FCSTD DOCUMENT  (FreeCAD 1.0R39319 (Git))
Label: main-assembly
License: All rights reserved
LicenseURL: http://en.wikipedia.org/wiki/All_rights_reserved
objects: App::Link×62, App::FeaturePython×6, Assembly::AssemblyLink×5, TechDraw::DrawViewImage×4, Assembly::JointGroup×1, Assembly::AssemblyObject×1, TechDraw::DrawSVGTemplate×1, TechDraw::DrawViewAnnotation×1, TechDraw::DrawPage×1
EXTERNAL_REF file=../sub-assemblies/legs.FCStd obj=Assembly
EXTERNAL_REF file=../sub-assemblies/legs.FCStd obj=steel_profile_40x40x400
EXTERNAL_REF file=../sub-assemblies/legs.FCStd obj=steel_profile_40x40x401
EXTERNAL_REF file=../sub-assemblies/legs.FCStd obj=steel_profile_40x40x402
EXTERNAL_REF file=../sub-assemblies/legs.FCStd obj=steel_profile_40x40x403
EXTERNAL_REF file=../sub-assemblies/legs.FCStd obj=steel_profile_40x40x404
EXTERNAL_REF file=../sub-assemblies/legs.FCStd obj=steel_profile_40x40x405
EXTERNAL_REF file=../sub-assemblies/legs.FCStd obj=steel_profile_40x40x406
EXTERNAL_REF file=../sub-assemblies/legs.FCStd obj=steel_profile_40x40x407
EXTERNAL_REF file=../sub-assemblies/legs.FCStd obj=steel_profile_40x40x408
EXTERNAL_REF file=../sub-assemblies/legs.FCStd obj=steel_profile_40x40x411
EXTERNAL_REF file=../sub-assemblies/legs.FCStd obj=steel_profile_40x40x412
EXTERNAL_REF file=../sub-assemblies/legs.FCStd obj=steel_profile_40x40x413
EXTERNAL_REF file=../sub-assemblies/legs.FCStd obj=steel_profile_40x40x414
EXTERNAL_REF file=../sub-assemblies/top-frame.FCStd obj=Assembly
EXTERNAL_REF file=../sub-assemblies/top-frame.FCStd obj=steel_profile_40x40x400
EXTERNAL_REF file=../sub-assemblies/top-frame.FCStd obj=steel_profile_40x40x401
EXTERNAL_REF file=../sub-assemblies/top-frame.FCStd obj=steel_profile_40x40x402
EXTERNAL_REF file=../sub-assemblies/top-frame.FCStd obj=steel_profile_40x40x403
EXTERNAL_REF file=../sub-assemblies/top-frame.FCStd obj=steel_profile_40x40x404
EXTERNAL_REF file=../sub-assemblies/top-frame.FCStd obj=steel_profile_40x40x405
EXTERNAL_REF file=../sub-assemblies/stepper-assembly.FCStd obj=Assembly
EXTERNAL_REF file=../sub-assemblies/stepper-assembly.FCStd obj=nema23_holder
EXTERNAL_REF file=../sub-assemblies/stepper-assembly.FCStd obj=Power_Step___PSM57HS2A54_2P
EXTERNAL_REF file=../sub-assemblies/stepper-assembly.FCStd obj=Coupler_6_35_8mm_Without_Screw
EXTERNAL_REF file=../sub-assemblies/stepper-assembly.FCStd obj=Part
EXTERNAL_REF file=../sub-assemblies/stepper-assembly.FCStd obj=ThreadedRod
EXTERNAL_REF file=../sub-assemblies/legs.FCStd obj=steel_profile_40x40x415
EXTERNAL_REF file=../sub-assemblies/legs.FCStd obj=x_stepper_mounting_profile
EXTERNAL_REF file=../sub-assemblies/stepper-assembly.FCStd obj=x_profile
EXTERNAL_REF file=../sub-assemblies/stepper-assembly.FCStd obj=Anti_Backlash_Nut_TR8x2
EXTERNAL_REF file=../sub-assemblies/stepper-assembly.FCStd obj=Part001
EXTERNAL_REF file=../sub-assemblies/stepper-assembly.FCStd obj=block_MGN9_H009
EXTERNAL_REF file=../sub-assemblies/stepper-assembly.FCStd obj=rail
EXTERNAL_REF file=../sub-assemblies/stepper-assembly.FCStd obj=MGN9_H
EXTERNAL_REF file=../sub-assemblies/stepper-assembly.FCStd obj=Part002
EXTERNAL_REF file=../sub-assemblies/top-frame.FCStd obj=steel_profile_40x40x406
EXTERNAL_REF file=../sub-assemblies/Y-stepper-assembly.FCStd obj=Assembly
EXTERNAL_REF file=../sub-assemblies/Y-stepper-assembly.FCStd obj=nema23_holder
EXTERNAL_REF file=../sub-assemblies/Y-stepper-assembly.FCStd obj=Power_Step___PSM57HS2A54_2P
EXTERNAL_REF file=../sub-assemblies/Y-stepper-assembly.FCStd obj=Coupler_6_35_8mm_Without_Screw
EXTERNAL_REF file=../sub-assemblies/Y-stepper-assembly.FCStd obj=Part
EXTERNAL_REF file=../sub-assemblies/Y-stepper-assembly.FCStd obj=ThreadedRod
EXTERNAL_REF file=../sub-assemblies/Y-stepper-assembly.FCStd obj=Anti_Backlash_Nut_TR8x2
EXTERNAL_REF file=../sub-assemblies/Y-stepper-assembly.FCStd obj=Part001
EXTERNAL_REF file=../sub-assemblies/Y-stepper-assembly.FCStd obj=MGN9_H
EXTERNAL_REF file=../sub-assemblies/Y-stepper-assembly.FCStd obj=Part002
EXTERNAL_REF file=../sub-assemblies/Y-stepper-assembly.FCStd obj=y_profile
EXTERNAL_REF file=../sub-assemblies/Z-stepper-assembly.FCStd obj=Assembly
EXTERNAL_REF file=../sub-assemblies/Z-stepper-assembly.FCStd obj=nema23_holder
EXTERNAL_REF file=../sub-assemblies/Z-stepper-assembly.FCStd obj=Power_Step___PSM57HS2A54_2P
EXTERNAL_REF file=../sub-assemblies/Z-stepper-assembly.FCStd obj=Coupler_6_35_8mm_Without_Screw
EXTERNAL_REF file=../sub-assemblies/Z-stepper-assembly.FCStd obj=Part
EXTERNAL_REF file=../sub-assemblies/Z-stepper-assembly.FCStd obj=ThreadedRod
EXTERNAL_REF file=../sub-assemblies/Z-stepper-assembly.FCStd obj=Anti_Backlash_Nut_TR8x2
EXTERNAL_REF file=../sub-assemblies/Z-stepper-assembly.FCStd obj=Part001
EXTERNAL_REF file=../sub-assemblies/Z-stepper-assembly.FCStd obj=MGN9_H
EXTERNAL_REF file=../sub-assemblies/Z-stepper-assembly.FCStd obj=Part002
EXTERNAL_REF file=../sub-assemblies/Z-stepper-assembly.FCStd obj=_0mm_motor_holder
EXTERNAL_REF file=../sub-assemblies/Z-stepper-assembly.FCStd obj=_0x40x100mm_profile
EXTERNAL_REF file=../sub-assemblies/Z-stepper-assembly.FCStd obj=Screw001
EXTERNAL_REF file=../sub-assemblies/Z-stepper-assembly.FCStd obj=Screw002
EXTERNAL_REF file=../sub-assemblies/Z-stepper-assembly.FCStd obj=M6x90_Screw_Copy
EXTERNAL_REF file=../sub-assemblies/Z-stepper-assembly.FCStd obj=M6x90_Screw_Copy001
EXTERNAL_REF file=../sub-assemblies/Z-stepper-assembly.FCStd obj=M6x90_Screw_Copy002
EXTERNAL_REF file=../sub-assemblies/Y-stepper-assembly.FCStd obj=_0x40x100mm_profile
EXTERNAL_REF file=../sub-assemblies/Y-stepper-assembly.FCStd obj=_0x40x100mm_profile001

FEATURE [App::Link] steel_profile_40x40x400  label="steel-profile-40x40x400"
  LinkPlacement = pos=(0,0,7.8701e-12) rot=(0,0,1;0rad)
  LinkedObject = -> <external ../sub-assemblies/legs.FCStd>#steel_profile_40x40x400
  Placement = pos=(0,0,7.8701e-12) rot=(0,0,1;0rad)
FEATURE [App::Link] steel_profile_40x40x401  label="steel-profile-40x40x401"
  LinkedObject = -> <external ../sub-assemblies/legs.FCStd>#steel_profile_40x40x401
FEATURE [App::Link] steel_profile_40x40x402  label="steel-profile-40x40x402"
  LinkPlacement = pos=(40,40,-9.72909e-07) rot=(0,0.707107,0.707107;3.14159rad)
  LinkedObject = -> <external ../sub-assemblies/legs.FCStd>#steel_profile_40x40x402
  Placement = pos=(40,40,-9.72909e-07) rot=(0,0.707107,0.707107;3.14159rad)
FEATURE [App::Link] steel_profile_40x40x403  label="steel-profile-40x40x403"
  LinkPlacement = pos=(-400,0,400) rot=(4.1e-05,1,0.000414;3.14076rad)
  LinkedObject = -> <external ../sub-assemblies/legs.FCStd>#steel_profile_40x40x403
  Placement = pos=(-400,0,400) rot=(4.1e-05,1,0.000414;3.14076rad)
FEATURE [App::Link] steel_profile_40x40x404  label="steel-profile-40x40x404"
  LinkPlacement = pos=(-440,440,0) rot=(0.99998,0.004685,0.004188;1.57079rad)
  LinkedObject = -> <external ../sub-assemblies/legs.FCStd>#steel_profile_40x40x404
  Placement = pos=(-440,440,0) rot=(0.99998,0.004685,0.004188;1.57079rad)
FEATURE [App::Link] steel_profile_40x40x405  label="steel-profile-40x40x405"
  LinkPlacement = pos=(0,440,0) rot=(0,0,1;0rad)
  LinkedObject = -> <external ../sub-assemblies/legs.FCStd>#steel_profile_40x40x405
  Placement = pos=(0,440,0) rot=(0,0,1;0rad)
FEATURE [App::Link] steel_profile_40x40x406  label="steel-profile-40x40x406"
  LinkPlacement = pos=(0,440,0) rot=(-0.003469,0.999988,-0.003488;4.71178rad)
  LinkedObject = -> <external ../sub-assemblies/legs.FCStd>#steel_profile_40x40x406
  Placement = pos=(0,440,0) rot=(-0.003469,0.999988,-0.003488;4.71178rad)
FEATURE [App::Link] steel_profile_40x40x407  label="steel-profile-40x40x407"
  LinkPlacement = pos=(-9.9e-15,1.7e-15,-3e-16) rot=(0.000745,0.999999,0.000745;4.71239rad)
  LinkedObject = -> <external ../sub-assemblies/legs.FCStd>#steel_profile_40x40x407
  Placement = pos=(-9.9e-15,1.7e-15,-3e-16) rot=(0.000745,0.999999,0.000745;4.71239rad)
FEATURE [App::Link] steel_profile_40x40x408  label="steel-profile-40x40x408"
  LinkPlacement = pos=(-440,440,0) rot=(-0.01966,0.055819,0.998247;0.008893rad)
  LinkedObject = -> <external ../sub-assemblies/legs.FCStd>#steel_profile_40x40x408
  Placement = pos=(-440,440,0) rot=(-0.01966,0.055819,0.998247;0.008893rad)
FEATURE [App::Link] steel_profile_40x40x411  label="steel-profile-40x40x411"
  LinkPlacement = pos=(0,440,360) rot=(0.000611,1,0.000434;4.71234rad)
  LinkedObject = -> <external ../sub-assemblies/legs.FCStd>#steel_profile_40x40x411
  Placement = pos=(0,440,360) rot=(0.000611,1,0.000434;4.71234rad)
FEATURE [App::Link] steel_profile_40x40x412  label="steel-profile-40x40x412"
  LinkPlacement = pos=(0,440,400) rot=(0.714086,0.000272,-0.713488;3.14225rad)
  LinkedObject = -> <external ../sub-assemblies/legs.FCStd>#steel_profile_40x40x412
  Placement = pos=(0,440,400) rot=(0.714086,0.000272,-0.713488;3.14225rad)
FEATURE [App::Link] steel_profile_40x40x413  label="steel-profile-40x40x413"
  LinkPlacement = pos=(0,0,360) rot=(-0.000373,1,0.000455;4.71239rad)
  LinkedObject = -> <external ../sub-assemblies/legs.FCStd>#steel_profile_40x40x413
  Placement = pos=(0,0,360) rot=(-0.000373,1,0.000455;4.71239rad)
FEATURE [App::Link] steel_profile_40x40x414  label="steel-profile-40x40x414"
  LinkPlacement = pos=(0,80,400.402) rot=(0.707403,0.000269,-0.706811;3.14225rad)
  LinkedObject = -> <external ../sub-assemblies/legs.FCStd>#steel_profile_40x40x414
  Placement = pos=(0,80,400.402) rot=(0.707403,0.000269,-0.706811;3.14225rad)
FEATURE [App::Link] steel_profile_40x40x415  label="steel-profile-40x40x415"
  LinkedObject = -> <external ../sub-assemblies/top-frame.FCStd>#steel_profile_40x40x400
FEATURE [App::Link] steel_profile_40x40x416  label="steel-profile-40x40x416"
  LinkPlacement = pos=(440,0,4e-05) rot=(0,0,1;0rad)
  LinkedObject = -> <external ../sub-assemblies/top-frame.FCStd>#steel_profile_40x40x401
  Placement = pos=(440,0,4e-05) rot=(0,0,1;0rad)
FEATURE [App::Link] steel_profile_40x40x417  label="steel-profile-40x40x417"
  LinkPlacement = pos=(0,440,0) rot=(0,0,1;0rad)
  LinkedObject = -> <external ../sub-assemblies/top-frame.FCStd>#steel_profile_40x40x402
  Placement = pos=(0,440,0) rot=(0,0,1;0rad)
FEATURE [App::Link] steel_profile_40x40x418  label="steel-profile-40x40x418"
  LinkPlacement = pos=(440,440,0) rot=(0,0,1;0rad)
  LinkedObject = -> <external ../sub-assemblies/top-frame.FCStd>#steel_profile_40x40x403
  Placement = pos=(440,440,0) rot=(0,0,1;0rad)
FEATURE [App::Link] steel_profile_40x40x419  label="steel-profile-40x40x419"
  LinkPlacement = pos=(40,40,376.43) rot=(0.57735,-0.57735,0.57735;4.18879rad)
  LinkedObject = -> <external ../sub-assemblies/top-frame.FCStd>#steel_profile_40x40x404
  Placement = pos=(40,40,376.43) rot=(0.57735,-0.57735,0.57735;4.18879rad)
FEATURE [App::Link] steel_profile_40x40x420  label="steel-profile-40x40x420"
  LinkPlacement = pos=(440,440,360) rot=(0,-1,0;1.5708rad)
  LinkedObject = -> <external ../sub-assemblies/top-frame.FCStd>#steel_profile_40x40x405
  Placement = pos=(440,440,360) rot=(0,-1,0;1.5708rad)
FEATURE [App::FeaturePython] Joint  label="Parallel"  # Assembly joint (typed FeaturePython)
  Activated = true
  AngleMax = 0
  AngleMin = 0
  Detach1 = false
  Detach2 = false
  Distance = 0
  Distance2 = 0
  EnableAngleMax = false
  EnableAngleMin = false
  EnableLengthMax = false
  EnableLengthMin = false
  JointType = 6 (Parallel)
  LengthMax = 0
  LengthMin = 0
  Placement1 = pos=(40,20,200) rot=(-0.57735,-0.57735,0.57735;2.0944rad)
  Placement2 = pos=(-1e-15,2,0) rot=(0.57735,-0.57735,0.57735;4.18879rad)
  Reference1 = -> Assembly [legs.steel_profile_40x40x400.Body.Face3,legs.steel_profile_40x40x400.Body.Face3]
  Reference2 = -> Assembly [Assembly001.steel_profile_40x40x417.Body.Face7,Assembly001.steel_profile_40x40x417.Body.Vertex15]
FEATURE [App::FeaturePython] Joint001  label="Parallel001"  # Assembly joint (typed FeaturePython)
  Activated = true
  AngleMax = 0
  AngleMin = 0
  Detach1 = false
  Detach2 = false
  Distance = 0
  Distance2 = 0
  EnableAngleMax = false
  EnableAngleMin = false
  EnableLengthMax = false
  EnableLengthMin = false
  JointType = 6 (Parallel)
  LengthMax = 0
  LengthMin = 0
  Placement1 = pos=(20,-9e-16,200) rot=(-1,0,0;1.5708rad)
  Placement2 = pos=(2,40,0) rot=(0,-0.707107,0.707107;3.14159rad)
  Reference1 = -> Assembly [legs.steel_profile_40x40x400.Body.Face1,legs.steel_profile_40x40x400.Body.Face1]
  Reference2 = -> Assembly [Assembly001.steel_profile_40x40x417.Body.Face5,Assembly001.steel_profile_40x40x417.Body.Vertex11]
FEATURE [App::FeaturePython] Joint002  label="Distance"  # Assembly joint (typed FeaturePython)
  Activated = true
  AngleMax = 0
  AngleMin = 0
  Detach1 = false
  Detach2 = false
  Distance = 0
  Distance2 = 0
  EnableAngleMax = false
  EnableAngleMin = false
  EnableLengthMax = false
  EnableLengthMin = false
  JointType = 5 (Distance)
  LengthMax = 0
  LengthMin = 0
  Placement1 = pos=(20,20,0) rot=(0,0,1;0rad)
  Placement2 = pos=(20,20,400) rot=(0,0,1;0rad)
  Reference1 = -> Assembly [Assembly001.steel_profile_40x40x417.Body.Face13,Assembly001.steel_profile_40x40x417.Body.Vertex21]
  Reference2 = -> Assembly [legs.steel_profile_40x40x400.Body.Face14,legs.steel_profile_40x40x400.Body.Vertex22]
FEATURE [App::FeaturePython] Joint003  label="Distance001"  # Assembly joint (typed FeaturePython)
  Activated = true
  AngleMax = 0
  AngleMin = 0
  Detach1 = false
  Detach2 = false
  Distance = 0
  Distance2 = 0
  EnableAngleMax = false
  EnableAngleMin = false
  EnableLengthMax = false
  EnableLengthMin = false
  JointType = 5 (Distance)
  LengthMax = 0
  LengthMin = 0
  Placement1 = pos=(20,-9e-16,200) rot=(-1,0,0;1.5708rad)
  Placement2 = pos=(20,40,200) rot=(0,-0.707107,0.707107;3.14159rad)
  Reference1 = -> Assembly [legs.steel_profile_40x40x400.Body.Face1,legs.steel_profile_40x40x400.Body.Vertex4]
  Reference2 = -> Assembly [Assembly001.steel_profile_40x40x417.Body.Face5,Assembly001.steel_profile_40x40x417.Body.Vertex11]
FEATURE [App::Link] nema23_holder  label="nema23-holder"
  LinkPlacement = pos=(0,0,0) rot=(-0.953069,0,-0.302943;2e-06rad)
  LinkedObject = -> <external ../sub-assemblies/stepper-assembly.FCStd>#nema23_holder
  Placement = pos=(0,0,0) rot=(-0.953069,0,-0.302943;2e-06rad)
FEATURE [App::Link] Power_Step___PSM57HS2A54_2P  label="Power Step - PSM57HS2A54-2P002"
  LinkPlacement = pos=(32.5,44.5,35.5) rot=(-2e-06,1,-4e-06;1.5708rad)
  LinkedObject = -> <external ../sub-assemblies/stepper-assembly.FCStd>#Power_Step___PSM57HS2A54_2P
  Placement = pos=(32.5,44.5,35.5) rot=(-2e-06,1,-4e-06;1.5708rad)
FEATURE [App::Link] Coupler_6_35_8mm_Without_Screw  label="Coupler 6.35-8mm Without Screw001"
  LinkPlacement = pos=(32.5,96.0278,35.5) rot=(0.993786,0.078707,-0.078701;1.57705rad)
  LinkedObject = -> <external ../sub-assemblies/stepper-assembly.FCStd>#Coupler_6_35_8mm_Without_Screw
  Placement = pos=(32.5,96.0278,35.5) rot=(0.993786,0.078707,-0.078701;1.57705rad)
FEATURE [App::Link] Part  label="bearing-support"
  LinkPlacement = pos=(32.498,479.614,35.5061) rot=(-1,-3e-06,3e-06;1.57078rad)
  LinkedObject = -> <external ../sub-assemblies/stepper-assembly.FCStd>#Part
  Placement = pos=(32.498,479.614,35.5061) rot=(-1,-3e-06,3e-06;1.57078rad)
FEATURE [App::Link] ThreadedRod  label="M8x400-ThreadedRod"
  LinkPlacement = pos=(32.5,94.614,35.5) rot=(-0.04014,0.706542,-0.706531;3.22182rad)
  LinkedObject = -> <external ../sub-assemblies/stepper-assembly.FCStd>#ThreadedRod
  Placement = pos=(32.5,94.614,35.5) rot=(-0.04014,0.706542,-0.706531;3.22182rad)
FEATURE [App::Link] steel_profile_40x40x421  label="steel-profile-40x40x421"
  LinkPlacement = pos=(-440,40,418.3) rot=(-0.999999,0,0;1.5708rad)
  LinkedObject = -> <external ../sub-assemblies/legs.FCStd>#steel_profile_40x40x415
  Placement = pos=(-440,40,418.3) rot=(-0.999999,0,0;1.5708rad)
FEATURE [App::Link] x_stepper_mounting_profile  label="x-stepper-mounting-profile"
  LinkPlacement = pos=(1.563e-13,440,354.54) rot=(0,0,-1;1.5708rad)
  LinkedObject = -> <external ../sub-assemblies/legs.FCStd>#x_stepper_mounting_profile
  Placement = pos=(1.563e-13,440,354.54) rot=(0,0,-1;1.5708rad)
FEATURE [Assembly::AssemblyLink] legs
  Group = -> [steel_profile_40x40x400,steel_profile_40x40x401,steel_profile_40x40x402,steel_profile_40x40x403,steel_profile_40x40x404,steel_profile_40x40x405,steel_profile_40x40x406,steel_profile_40x40x407,steel_profile_40x40x408,steel_profile_40x40x411,steel_profile_40x40x412,steel_profile_40x40x413,steel_profile_40x40x414,steel_profile_40x40x421,x_stepper_mounting_profile]
  LinkedObject = -> <external ../sub-assemblies/legs.FCStd>#Assembly
  Origin = -> Origin001
  Rigid = true
FEATURE [App::FeaturePython] GroundedJoint  # Assembly grounded joint (typed FeaturePython)
  ObjectToGround = -> legs
FEATURE [App::Link] x_profile  label="x-profile"
  LinkPlacement = pos=(-167.5,276.601,55.7999) rot=(-0.577347,0.577348,0.577356;2.09438rad)
  LinkedObject = -> <external ../sub-assemblies/stepper-assembly.FCStd>#x_profile
  Placement = pos=(-167.5,276.601,55.7999) rot=(-0.577347,0.577348,0.577356;2.09438rad)
FEATURE [App::Link] Anti_Backlash_Nut_TR8x2  label="Anti-Backlash_Nut_TR8x005"
  LinkPlacement = pos=(32.5,316.91,35.5) rot=(0,1,0;0rad)
  LinkedObject = -> <external ../sub-assemblies/stepper-assembly.FCStd>#Anti_Backlash_Nut_TR8x2
  Placement = pos=(32.5,316.91,35.5) rot=(0,1,0;0rad)
FEATURE [App::Link] Part001  label="Nut-TR8"
  LinkPlacement = pos=(32.4991,261.601,35.5026) rot=(-0.577351,0.577355,-0.577345;4.18878rad)
  LinkedObject = -> <external ../sub-assemblies/stepper-assembly.FCStd>#Part001
  Placement = pos=(32.4991,261.601,35.5026) rot=(-0.577351,0.577355,-0.577345;4.18878rad)
FEATURE [App::Link] block_MGN9_H009  label="block-MGN9-H010"
  LinkPlacement = pos=(214.983,296.784,11.8004) rot=(1,-1e-06,-1e-06;1.57081rad)
  LinkedObject = -> <external ../sub-assemblies/stepper-assembly.FCStd>#block_MGN9_H009
  Placement = pos=(214.983,296.784,11.8004) rot=(1,-1e-06,-1e-06;1.57081rad)
FEATURE [App::Link] rail  label="rail001"
  LinkPlacement = pos=(214.965,441.284,9.01518) rot=(1,-1e-06,-1e-06;1.57081rad)
  LinkedObject = -> <external ../sub-assemblies/stepper-assembly.FCStd>#rail
  Placement = pos=(214.965,441.284,9.01518) rot=(1,-1e-06,-1e-06;1.57081rad)
FEATURE [App::Link] MGN9_H  label="block-MGN9-H009"
  LinkPlacement = pos=(-149.71,296.602,11.8002) rot=(1e-06,0.781989,0.782002;3.14159rad)
  LinkedObject = -> <external ../sub-assemblies/stepper-assembly.FCStd>#MGN9_H
  Placement = pos=(-149.71,296.602,11.8002) rot=(1e-06,0.781989,0.782002;3.14159rad)
FEATURE [App::Link] Part002  label="rail"
  LinkPlacement = pos=(-149.691,441.102,8.99001) rot=(1,-1e-06,-1e-06;1.57081rad)
  LinkedObject = -> <external ../sub-assemblies/stepper-assembly.FCStd>#Part002
  Placement = pos=(-149.691,441.102,8.99001) rot=(1,-1e-06,-1e-06;1.57081rad)
FEATURE [Assembly::AssemblyLink] stepper_assembly  label="stepper-assembly"
  Group = -> [nema23_holder,Power_Step___PSM57HS2A54_2P,Coupler_6_35_8mm_Without_Screw,Part,ThreadedRod,x_profile,Anti_Backlash_Nut_TR8x2,Part001,block_MGN9_H009,rail,MGN9_H,Part002]
  LinkedObject = -> <external ../sub-assemblies/stepper-assembly.FCStd>#Assembly
  Origin = -> Origin003
  Placement = pos=(60,207.5,394.54) rot=(0,0,1;1.5708rad)
  Rigid = true
FEATURE [App::Link] steel_profile_40x40x422  label="steel-profile-40x40x422"
  LinkPlacement = pos=(3,40,400) rot=(1,0,0;4.71239rad)
  LinkedObject = -> <external ../sub-assemblies/top-frame.FCStd>#steel_profile_40x40x406
  Placement = pos=(3,40,400) rot=(1,0,0;4.71239rad)
FEATURE [Assembly::AssemblyLink] Assembly001  label="top-frame"
  Group = -> [steel_profile_40x40x415,steel_profile_40x40x416,steel_profile_40x40x417,steel_profile_40x40x418,steel_profile_40x40x419,steel_profile_40x40x420,steel_profile_40x40x422]
  LinkedObject = -> <external ../sub-assemblies/top-frame.FCStd>#Assembly
  Origin = -> Origin002
  Placement = pos=(40,480,400) rot=(0,0,1;3.14159rad)
  Rigid = true
FEATURE [App::Link] nema23_holder001  label="nema23-holder001"
  LinkPlacement = pos=(0,0,0) rot=(-0.952988,0,-0.302917;2e-06rad)
  LinkedObject = -> <external ../sub-assemblies/Y-stepper-assembly.FCStd>#nema23_holder
  Placement = pos=(0,0,0) rot=(-0.952988,0,-0.302917;2e-06rad)
FEATURE [App::Link] Power_Step___PSM57HS2A54_2P001  label="Power Step - PSM57HS2A54-2P003"
  LinkPlacement = pos=(32.5,44.5,35.5) rot=(-2e-06,1,-4e-06;1.5708rad)
  LinkedObject = -> <external ../sub-assemblies/Y-stepper-assembly.FCStd>#Power_Step___PSM57HS2A54_2P
  Placement = pos=(32.5,44.5,35.5) rot=(-2e-06,1,-4e-06;1.5708rad)
FEATURE [App::Link] Coupler_6_35_8mm_Without_Screw001  label="Coupler 6.35-8mm Without Screw002"
  LinkPlacement = pos=(32.5,96.0278,35.5) rot=(0.993786,0.078707,-0.078701;1.57705rad)
  LinkedObject = -> <external ../sub-assemblies/Y-stepper-assembly.FCStd>#Coupler_6_35_8mm_Without_Screw
  Placement = pos=(32.5,96.0278,35.5) rot=(0.993786,0.078707,-0.078701;1.57705rad)
FEATURE [App::Link] Part003  label="bearing-support001"
  LinkPlacement = pos=(32.498,479.614,35.5061) rot=(-1,-3e-06,3e-06;1.57078rad)
  LinkedObject = -> <external ../sub-assemblies/Y-stepper-assembly.FCStd>#Part
  Placement = pos=(32.498,479.614,35.5061) rot=(-1,-3e-06,3e-06;1.57078rad)
FEATURE [App::Link] ThreadedRod001  label="M8x400-ThreadedRod001"
  LinkPlacement = pos=(32.5,94.614,35.5) rot=(-0.04014,0.706542,-0.706531;3.22182rad)
  LinkedObject = -> <external ../sub-assemblies/Y-stepper-assembly.FCStd>#ThreadedRod
  Placement = pos=(32.5,94.614,35.5) rot=(-0.04014,0.706542,-0.706531;3.22182rad)
FEATURE [App::Link] Anti_Backlash_Nut_TR8x003  label="Anti-Backlash_Nut_TR8x006"
  LinkPlacement = pos=(32.5,316.91,35.5) rot=(0,1,0;0rad)
  LinkedObject = -> <external ../sub-assemblies/Y-stepper-assembly.FCStd>#Anti_Backlash_Nut_TR8x2
  Placement = pos=(32.5,316.91,35.5) rot=(0,1,0;0rad)
FEATURE [App::Link] Part004  label="Nut-TR009"
  LinkPlacement = pos=(32.4991,261.601,35.5026) rot=(0.577353,-0.577352,0.577346;2.09441rad)
  LinkedObject = -> <external ../sub-assemblies/Y-stepper-assembly.FCStd>#Part001
  Placement = pos=(32.4991,261.601,35.5026) rot=(0.577353,-0.577352,0.577346;2.09441rad)
FEATURE [App::Link] MGN9_H001  label="block-MGN9-H011"
  LinkPlacement = pos=(8.50001,296.601,3.00315) rot=(-0.595349,-0.595353,-0.595359;2.09438rad)
  LinkedObject = -> <external ../sub-assemblies/Y-stepper-assembly.FCStd>#MGN9_H
  Placement = pos=(8.50001,296.601,3.00315) rot=(-0.595349,-0.595353,-0.595359;2.09438rad)
FEATURE [App::Link] Part005  label="rail002"
  LinkPlacement = pos=(5.68728,190.892,3.01962) rot=(0.595351,0.595349,0.595361;4.1888rad)
  LinkedObject = -> <external ../sub-assemblies/Y-stepper-assembly.FCStd>#Part002
  Placement = pos=(5.68728,190.892,3.01962) rot=(0.595351,0.595349,0.595361;4.1888rad)
FEATURE [App::FeaturePython] Joint004  label="Distance002"  # Assembly joint (typed FeaturePython)
  Activated = true
  AngleMax = 0
  AngleMin = 0
  Detach1 = false
  Detach2 = false
  Distance = 0
  Distance2 = 0
  EnableAngleMax = false
  EnableAngleMin = false
  EnableLengthMax = false
  EnableLengthMin = false
  JointType = 5 (Distance)
  LengthMax = 0
  LengthMin = 0
  Placement1 = pos=(20,-9e-16,200) rot=(-1,0,0;1.5708rad)
  Placement2 = pos=(32.5,36.1951,0) rot=(0,0,1;0rad)
  Reference1 = -> Assembly [Assembly001.steel_profile_40x40x419.Body.Face1,Assembly001.steel_profile_40x40x419.Body.Vertex1]
  Reference2 = -> Assembly [Y_stepper_assembly.nema23_holder001.Body.Face15,Y_stepper_assembly.nema23_holder001.Body.Edge13]
FEATURE [Assembly::JointGroup] Joints
  Group = -> [GroundedJoint,Joint,Joint001,Joint002,Joint003,Joint004]
FEATURE [App::Link] y_profile  label="y-profile"
  LinkPlacement = pos=(52.4989,316.604,-164.497) rot=(-2e-06,0.729162,-0.72915;3.14159rad)
  LinkedObject = -> <external ../sub-assemblies/Y-stepper-assembly.FCStd>#y_profile
  Placement = pos=(52.4989,316.604,-164.497) rot=(-2e-06,0.729162,-0.72915;3.14159rad)
FEATURE [App::Link] nema23_holder002  label="nema23-holder002"
  LinkPlacement = pos=(-8e-15,0,5.51e-14) rot=(-0.953074,-1.1e-05,-0.302948;2e-06rad)
  LinkedObject = -> <external ../sub-assemblies/Z-stepper-assembly.FCStd>#nema23_holder
  Placement = pos=(-8e-15,0,5.51e-14) rot=(-0.953074,-1.1e-05,-0.302948;2e-06rad)
FEATURE [App::Link] Power_Step___PSM57HS2A54_2P002  label="Power Step - PSM57HS2A54-2P004"
  LinkPlacement = pos=(32.5,44.5,35.5) rot=(-2e-06,1,-4e-06;1.5708rad)
  LinkedObject = -> <external ../sub-assemblies/Z-stepper-assembly.FCStd>#Power_Step___PSM57HS2A54_2P
  Placement = pos=(32.5,44.5,35.5) rot=(-2e-06,1,-4e-06;1.5708rad)
FEATURE [App::Link] Coupler_6_35_8mm_Without_Screw002  label="Coupler 6.35-8mm Without Screw003"
  LinkPlacement = pos=(32.5,96.0278,35.5) rot=(0.993786,0.078707,-0.078701;1.57705rad)
  LinkedObject = -> <external ../sub-assemblies/Z-stepper-assembly.FCStd>#Coupler_6_35_8mm_Without_Screw
  Placement = pos=(32.5,96.0278,35.5) rot=(0.993786,0.078707,-0.078701;1.57705rad)
FEATURE [App::Link] Part006  label="bearing-support002"
  LinkPlacement = pos=(32.498,479.614,35.5061) rot=(-1,-3e-06,3e-06;1.57078rad)
  LinkedObject = -> <external ../sub-assemblies/Z-stepper-assembly.FCStd>#Part
  Placement = pos=(32.498,479.614,35.5061) rot=(-1,-3e-06,3e-06;1.57078rad)
FEATURE [App::Link] ThreadedRod002  label="M8x400-ThreadedRod002"
  LinkPlacement = pos=(32.5,94.614,35.5) rot=(-0.04014,0.706542,-0.706531;3.22182rad)
  LinkedObject = -> <external ../sub-assemblies/Z-stepper-assembly.FCStd>#ThreadedRod
  Placement = pos=(32.5,94.614,35.5) rot=(-0.04014,0.706542,-0.706531;3.22182rad)
FEATURE [App::Link] Anti_Backlash_Nut_TR8x004  label="Anti-Backlash_Nut_TR8x007"
  LinkPlacement = pos=(32.5,316.91,35.5) rot=(0,1,0;0rad)
  LinkedObject = -> <external ../sub-assemblies/Z-stepper-assembly.FCStd>#Anti_Backlash_Nut_TR8x2
  Placement = pos=(32.5,316.91,35.5) rot=(0,1,0;0rad)
FEATURE [App::Link] Part007  label="Nut-TR010"
  LinkPlacement = pos=(32.4991,261.601,35.5026) rot=(0.577353,-0.577352,0.577346;2.09441rad)
  LinkedObject = -> <external ../sub-assemblies/Z-stepper-assembly.FCStd>#Part001
  Placement = pos=(32.4991,261.601,35.5026) rot=(0.577353,-0.577352,0.577346;2.09441rad)
FEATURE [App::Link] MGN9_H002  label="block-MGN9-H012"
  LinkPlacement = pos=(33.1028,297.601,10.4187) rot=(-1e-06,-0.707104,-0.70711;3.1416rad)
  LinkedObject = -> <external ../sub-assemblies/Z-stepper-assembly.FCStd>#MGN9_H
  Placement = pos=(33.1028,297.601,10.4187) rot=(-1e-06,-0.707104,-0.70711;3.1416rad)
FEATURE [App::Link] Part008  label="rail003"
  LinkPlacement = pos=(33.0843,191.891,7.60456) rot=(1e-06,0.707101,0.707112;3.14159rad)
  LinkedObject = -> <external ../sub-assemblies/Z-stepper-assembly.FCStd>#Part002
  Placement = pos=(33.0843,191.891,7.60456) rot=(1e-06,0.707101,0.707112;3.14159rad)
FEATURE [App::Link] _0mm_motor_holder  label="80mm-motor-holder"
  LinkPlacement = pos=(34.5,276.5,55) rot=(0,0.707107,0.707107;3.14159rad)
  LinkedObject = -> <external ../sub-assemblies/Z-stepper-assembly.FCStd>#_0mm_motor_holder
  Placement = pos=(34.5,276.5,55) rot=(0,0.707107,0.707107;3.14159rad)
FEATURE [App::Link] _0x40x100mm_profile  label="40x40x100mm-profile"
  LinkPlacement = pos=(84.5,276.5,15) rot=(0,-1,0;1.5708rad)
  LinkedObject = -> <external ../sub-assemblies/Z-stepper-assembly.FCStd>#_0x40x100mm_profile
  Placement = pos=(84.5,276.5,15) rot=(0,-1,0;1.5708rad)
FEATURE [App::Link] Screw001  label="M6x90-Screw"
  LinkPlacement = pos=(-10.5,282.5,134.5) rot=(0.619938,-0.784651,0;0rad)
  LinkedObject = -> <external ../sub-assemblies/Z-stepper-assembly.FCStd>#Screw001
  Placement = pos=(-10.5,282.5,134.5) rot=(0.619938,-0.784651,0;0rad)
FEATURE [App::Link] Screw002  label="M6x90-Screw001"
  LinkPlacement = pos=(-10.5,312.5,134.5) rot=(0.619938,-0.784651,0;0rad)
  LinkedObject = -> <external ../sub-assemblies/Z-stepper-assembly.FCStd>#Screw002
  Placement = pos=(-10.5,312.5,134.5) rot=(0.619938,-0.784651,0;0rad)
FEATURE [App::Link] M6x90_Screw_Copy
  LinkPlacement = pos=(79.5,282.5,134.6) rot=(0,0,1;3.14159rad)
  LinkedObject = -> <external ../sub-assemblies/Z-stepper-assembly.FCStd>#M6x90_Screw_Copy
  Placement = pos=(79.5,282.5,134.6) rot=(0,0,1;3.14159rad)
FEATURE [App::Link] M6x90_Screw_Copy001
  LinkPlacement = pos=(79.5,312.5,134.6) rot=(0,0,1;3.14159rad)
  LinkedObject = -> <external ../sub-assemblies/Z-stepper-assembly.FCStd>#M6x90_Screw_Copy001
  Placement = pos=(79.5,312.5,134.6) rot=(0,0,1;3.14159rad)
FEATURE [App::Link] M6x90_Screw_Copy002
  LinkPlacement = pos=(-10.5,282.5,134.5) rot=(0.619938,-0.784651,0;0rad)
  LinkedObject = -> <external ../sub-assemblies/Z-stepper-assembly.FCStd>#M6x90_Screw_Copy002
  Placement = pos=(-10.5,282.5,134.5) rot=(0.619938,-0.784651,0;0rad)
FEATURE [Assembly::AssemblyLink] Z_stepper_assembly  label="Z-stepper-assembly"
  Group = -> [nema23_holder002,Power_Step___PSM57HS2A54_2P002,Coupler_6_35_8mm_Without_Screw002,Part006,ThreadedRod002,Anti_Backlash_Nut_TR8x004,Part007,MGN9_H002,Part008,_0mm_motor_holder,_0x40x100mm_profile,Screw001,Screw002,M6x90_Screw_Copy,M6x90_Screw_Copy001,M6x90_Screw_Copy002]
  LinkedObject = -> <external ../sub-assemblies/Z-stepper-assembly.FCStd>#Assembly
  Origin = -> Origin005
  Placement = pos=(-48.7667,173.258,1086.28) rot=(-0.57735,-0.57735,0.57735;2.0944rad)
  Rigid = true
FEATURE [App::Link] _0x40x100mm_profile001  label="40x40x100mm-profile001"
  LinkPlacement = pos=(8.7489,348.05,235.362) rot=(1,0,0;1.5708rad)
  LinkedObject = -> <external ../sub-assemblies/Y-stepper-assembly.FCStd>#_0x40x100mm_profile
  Placement = pos=(8.7489,348.05,235.362) rot=(1,0,0;1.5708rad)
FEATURE [App::Link] _0x40x100mm_profile002  label="40x40x100mm-profile002"
  LinkPlacement = pos=(32,243,-164) rot=(-1,0,0;1.5708rad)
  LinkedObject = -> <external ../sub-assemblies/Y-stepper-assembly.FCStd>#_0x40x100mm_profile001
  Placement = pos=(32,243,-164) rot=(-1,0,0;1.5708rad)
FEATURE [Assembly::AssemblyLink] Y_stepper_assembly  label="Y-stepper-assembly"
  Group = -> [nema23_holder001,Power_Step___PSM57HS2A54_2P001,Coupler_6_35_8mm_Without_Screw001,Part003,ThreadedRod001,Anti_Backlash_Nut_TR8x003,Part004,MGN9_H001,Part005,y_profile,_0x40x100mm_profile001,_0x40x100mm_profile002]
  LinkedObject = -> <external ../sub-assemblies/Y-stepper-assembly.FCStd>#Assembly
  Origin = -> Origin004
  Placement = pos=(-0.612144,502.308,776.43) rot=(0,1e-06,1;3.14159rad)
  Rigid = true
FEATURE [Assembly::AssemblyObject] Assembly
  Group = -> [Joints,legs,GroundedJoint,Assembly001,Joint,Joint001,Joint002,Joint003,stepper_assembly,Y_stepper_assembly,Joint004,Z_stepper_assembly]
  Origin = -> Origin
  Type = Assembly
FEATURE [TechDraw::DrawSVGTemplate] Template
  Height = 210
  Orientation = 1
  Template = <path>
  Width = 297
FEATURE [TechDraw::DrawViewImage] ActiveView001  label="Y"
  Height = 102.4
  ImageFile = <userpath>/.cache/FreeCAD/Cache/FreeCAD_Doc_1507e429-804d-4e93-ae59-f7ba2e4ac061_45bff6_36913/PageActiveView001rUnWWh.png
  LockPosition = false
  Rotation = 0
  ScaleType = 2
  Width = 128
  X = 254.231
  Y = 68.2217
FEATURE [TechDraw::DrawViewImage] ActiveView002  label="Z"
  Height = 102.4
  ImageFile = <userpath>/.cache/FreeCAD/Cache/FreeCAD_Doc_1507e429-804d-4e93-ae59-f7ba2e4ac061_df227c_36913/PageActiveView5mA7Qo.png
  LockPosition = false
  Rotation = 0
  ScaleType = 2
  Width = 128
  X = 175.736
  Y = 60.7246
FEATURE [TechDraw::DrawViewImage] ActiveView  label="X"
  Height = 102.4
  ImageFile = <userpath>/.cache/FreeCAD/Cache/FreeCAD_Doc_1507e429-804d-4e93-ae59-f7ba2e4ac061_0c7716_36913/PageActiveViewThDkJc.png
  LockPosition = false
  Rotation = 0
  ScaleType = 2
  Width = 128
  X = 216.072
  Y = 162.108
FEATURE [TechDraw::DrawViewImage] ActiveView003
  Height = 102.4
  ImageFile = <userpath>/.cache/FreeCAD/Cache/FreeCAD_Doc_a727402a-c459-441b-822e-c6c33594917e_9b285e_36913/PageActiveView003J3glPR.png
  LockPosition = false
  Rotation = 0
  Scale = 2
  ScaleType = 2
  Width = 128
  X = 64.5788
  Y = 92.8871
FEATURE [TechDraw::DrawViewAnnotation] Annotation
  Font = osifont
  LineSpace = 100
  LockPosition = false
  MaxWidth = -1
  Rotation = 0
  ScaleType = 0
  Text = VE1 CNC mill | Open Hardware CERN-OHL-S version 2
  TextSize = 7
  TextStyle = 0
  X = 81.2526
  Y = 194.504
FEATURE [TechDraw::DrawPage] Page
  KeepUpdated = true
  NextBalloonIndex = 1
  ProjectionType = 0
  Template = -> Template
  Views = -> [ActiveView001,ActiveView002,ActiveView,ActiveView003,Annotation]
note: 1 file-system path scrubbed to <path> (originals preserved in the JSON sidecar)

RESOLVED EXTERNAL PARTS (link-assembly join: the EXTERNAL_REF files above that resolve inside this repo's crawl, each included once):
---- part ../sub-assemblies/legs.FCStd = doc fcstd_d6a536308a57 ----
FCSTD DOCUMENT  (FreeCAD 1.0R39319 (Git))
Label: legs
License: All rights reserved
LicenseURL: http://en.wikipedia.org/wiki/All_rights_reserved
objects: App::FeaturePython×23, App::Link×15, Assembly::JointGroup×1, Assembly::AssemblyObject×1
EXTERNAL_REF file=../parts/steel-profile-40x40x400.FCStd obj=Part
EXTERNAL_REF file=../parts/x-stepper-mounting-profile.FCStd obj=Part

FEATURE [App::Link] steel_profile_40x40x400  label="steel-profile-40x40x400"
  LinkPlacement = pos=(0,0,7.8701e-12) rot=(0,0,1;0rad)
  LinkedObject = -> <external ../parts/steel-profile-40x40x400.FCStd>#Part
  Placement = pos=(0,0,7.8701e-12) rot=(0,0,1;0rad)
FEATURE [App::FeaturePython] GroundedJoint  # Assembly grounded joint (typed FeaturePython)
  ObjectToGround = -> steel_profile_40x40x400
  Placement = pos=(0,0,7.8701e-12) rot=(0,0,1;0rad)
FEATURE [App::Link] steel_profile_40x40x401  label="steel-profile-40x40x401"
  LinkedObject = -> <external ../parts/steel-profile-40x40x400.FCStd>#Part
FEATURE [App::Link] steel_profile_40x40x402  label="steel-profile-40x40x402"
  LinkPlacement = pos=(40,40,-9.72909e-07) rot=(0,0.707107,0.707107;3.14159rad)
  LinkedObject = -> <external ../parts/steel-profile-40x40x400.FCStd>#Part
  Placement = pos=(40,40,-9.72909e-07) rot=(0,0.707107,0.707107;3.14159rad)
FEATURE [App::Link] steel_profile_40x40x403  label="steel-profile-40x40x403"
  LinkPlacement = pos=(-400,0,400) rot=(4.1e-05,1,0.000414;3.14076rad)
  LinkedObject = -> <external ../parts/steel-profile-40x40x400.FCStd>#Part
  Placement = pos=(-400,0,400) rot=(4.1e-05,1,0.000414;3.14076rad)
FEATURE [App::Link] steel_profile_40x40x404  label="steel-profile-40x40x404"
  LinkPlacement = pos=(-440,440,0) rot=(0.99998,0.004685,0.004188;1.57079rad)
  LinkedObject = -> <external ../parts/steel-profile-40x40x400.FCStd>#Part
  Placement = pos=(-440,440,0) rot=(0.99998,0.004685,0.004188;1.57079rad)
FEATURE [App::Link] steel_profile_40x40x405  label="steel-profile-40x40x405"
  LinkPlacement = pos=(0,440,0) rot=(0,0,1;0rad)
  LinkedObject = -> <external ../parts/steel-profile-40x40x400.FCStd>#Part
  Placement = pos=(0,440,0) rot=(0,0,1;0rad)
FEATURE [App::Link] steel_profile_40x40x406  label="steel-profile-40x40x406"
  LinkPlacement = pos=(0,440,0) rot=(-0.003469,0.999988,-0.003488;4.71178rad)
  LinkedObject = -> <external ../parts/steel-profile-40x40x400.FCStd>#Part
  Placement = pos=(0,440,0) rot=(-0.003469,0.999988,-0.003488;4.71178rad)
FEATURE [App::Link] steel_profile_40x40x407  label="steel-profile-40x40x407"
  LinkPlacement = pos=(-9.9e-15,1.7e-15,-3e-16) rot=(0.000745,0.999999,0.000745;4.71239rad)
  LinkedObject = -> <external ../parts/steel-profile-40x40x400.FCStd>#Part
  Placement = pos=(-9.9e-15,1.7e-15,-3e-16) rot=(0.000745,0.999999,0.000745;4.71239rad)
FEATURE [App::FeaturePython] GroundedJoint001  # Assembly grounded joint (typed FeaturePython)
  ObjectToGround = -> steel_profile_40x40x402
  Placement = pos=(40,40,-9.72909e-07) rot=(0,0.707107,0.707107;3.14159rad)
FEATURE [App::FeaturePython] GroundedJoint002  # Assembly grounded joint (typed FeaturePython)
  ObjectToGround = -> steel_profile_40x40x407
  Placement = pos=(-9.9e-15,1.7e-15,-3e-16) rot=(0.000745,0.999999,0.000745;4.71239rad)
FEATURE [App::FeaturePython] GroundedJoint003  # Assembly grounded joint (typed FeaturePython)
  ObjectToGround = -> steel_profile_40x40x405
  Placement = pos=(8.20807e-06,440,-1.75932e-05) rot=(0,0,1;0rad)
FEATURE [App::FeaturePython] GroundedJoint004  # Assembly grounded joint (typed FeaturePython)
  ObjectToGround = -> steel_profile_40x40x406
  Placement = pos=(3.27425e-05,440,1.2557e-05) rot=(-0.003469,0.999988,-0.003488;4.71178rad)
FEATURE [App::FeaturePython] Joint  label="Distance"  # Assembly joint (typed FeaturePython)
  Activated = true
  AngleMax = 0
  AngleMin = 0
  Detach1 = false
  Detach2 = false
  Distance = 0
  Distance2 = 0
  EnableAngleMax = false
  EnableAngleMin = false
  EnableLengthMax = false
  EnableLengthMin = false
  JointType = 5 (Distance)
  LengthMax = 0
  LengthMin = 0
  Placement1 = pos=(40,20,200) rot=(-0.57735,-0.57735,0.57735;2.0944rad)
  Placement2 = pos=(20,20,400) rot=(0,0,1;0rad)
  Reference1 = -> Assembly [steel_profile_40x40x404.Body.Face3,steel_profile_40x40x404.Body.Vertex5]
  Reference2 = -> Assembly [steel_profile_40x40x406.Body.Face14,steel_profile_40x40x406.Body.Vertex18]
FEATURE [App::FeaturePython] Joint001  label="Distance001"  # Assembly joint (typed FeaturePython)
  Activated = true
  AngleMax = 0
  AngleMin = 0
  Detach1 = false
  Detach2 = false
  Distance = 0
  Distance2 = 0
  EnableAngleMax = false
  EnableAngleMin = false
  EnableLengthMax = false
  EnableLengthMin = false
  JointType = 5 (Distance)
  LengthMax = 0
  LengthMin = 0
  Placement1 = pos=(20,20,400) rot=(0,0,1;0rad)
  Placement2 = pos=(20,40,200) rot=(0,-0.707107,0.707107;3.14159rad)
  Reference1 = -> Assembly [steel_profile_40x40x404.Body.Face14,steel_profile_40x40x404.Body.Vertex22]
  Reference2 = -> Assembly [steel_profile_40x40x403.Body.Face5,steel_profile_40x40x403.Body.Vertex9]
FEATURE [App::FeaturePython] Joint002  label="Parallel"  # Assembly joint (typed FeaturePython)
  Activated = true
  AngleMax = 0
  AngleMin = 0
  Detach1 = false
  Detach2 = false
  Distance = 0
  Distance2 = 0
  EnableAngleMax = false
  EnableAngleMin = false
  EnableLengthMax = false
  EnableLengthMin = false
  JointType = 6 (Parallel)
  LengthMax = 0
  LengthMin = 0
  Placement1 = pos=(2,40,0) rot=(0,-0.707107,0.707107;3.14159rad)
  Placement2 = pos=(40,2,400) rot=(-0.57735,-0.57735,0.57735;2.0944rad)
  Reference1 = -> Assembly [steel_profile_40x40x404.Body.Face5,steel_profile_40x40x404.Body.Vertex11]
  Reference2 = -> Assembly [steel_profile_40x40x406.Body.Face3,steel_profile_40x40x406.Body.Vertex6]
FEATURE [App::FeaturePython] Joint003  label="Distance002"  # Assembly joint (typed FeaturePython)
  Activated = true
  AngleMax = 0
  AngleMin = 0
  Detach1 = false
  Detach2 = false
  Distance = 0
  Distance2 = 0
  EnableAngleMax = false
  EnableAngleMin = false
  EnableLengthMax = false
  EnableLengthMin = false
  JointType = 5 (Distance)
  LengthMax = 0
  LengthMin = 0
  Placement1 = pos=(20,-9e-16,200) rot=(-1,0,0;1.5708rad)
  Placement2 = pos=(20,20,400) rot=(0,0,1;0rad)
  Reference1 = -> Assembly [steel_profile_40x40x404.Body.Face1,steel_profile_40x40x404.Body.Vertex4]
  Reference2 = -> Assembly [steel_profile_40x40x403.Body.Face14,steel_profile_40x40x403.Body.Vertex22]
FEATURE [App::FeaturePython] Joint004  label="Distance003"  # Assembly joint (typed FeaturePython)
  Activated = true
  AngleMax = 0
  AngleMin = 0
  Detach1 = false
  Detach2 = false
  Distance = 0
  Distance2 = 0
  EnableAngleMax = false
  EnableAngleMin = false
  EnableLengthMax = false
  EnableLengthMin = false
  JointType = 5 (Distance)
  LengthMax = 0
  LengthMin = 0
  Placement1 = pos=(20,40,200) rot=(0,-0.707107,0.707107;3.14159rad)
  Placement2 = pos=(40,20,200) rot=(-0.57735,-0.57735,0.57735;2.0944rad)
  Reference1 = -> Assembly [steel_profile_40x40x404.Body.Face5,steel_profile_40x40x404.Body.Face5]
  Reference2 = -> Assembly [steel_profile_40x40x406.Body.Face3,steel_profile_40x40x406.Body.Vertex6]
FEATURE [App::FeaturePython] Joint005  label="Distance004"  # Assembly joint (typed FeaturePython)
  Activated = true
  AngleMax = 0
  AngleMin = 0
  Detach1 = false
  Detach2 = false
  Distance = 0
  Distance2 = 0
  EnableAngleMax = false
  EnableAngleMin = false
  EnableLengthMax = false
  EnableLengthMin = false
  JointType = 5 (Distance)
  LengthMax = 0
  LengthMin = 0
  Placement1 = pos=(20,-9e-16,200) rot=(-1,0,0;1.5708rad)
  Placement2 = pos=(20,-9e-16,200) rot=(-1,0,0;1.5708rad)
  Reference1 = -> Assembly [steel_profile_40x40x403.Body.Face1,steel_profile_40x40x403.Body.Vertex4]
  Reference2 = -> Assembly [steel_profile_40x40x407.Body.Face1,steel_profile_40x40x407.Body.Vertex2]
FEATURE [App::FeaturePython] GroundedJoint005  # Assembly grounded joint (typed FeaturePython)
  ObjectToGround = -> steel_profile_40x40x404
  Placement = pos=(-440,440,-5.91282e-05) rot=(0.99998,0.004685,0.004188;1.57079rad)
FEATURE [App::FeaturePython] GroundedJoint006  # Assembly grounded joint (typed FeaturePython)
  ObjectToGround = -> steel_profile_40x40x403
  Placement = pos=(-400,-1.1921e-05,400) rot=(4.1e-05,1,0.000414;3.14076rad)
FEATURE [App::Link] steel_profile_40x40x408  label="steel-profile-40x40x408"
  LinkPlacement = pos=(-440,440,0) rot=(-0.01966,0.055819,0.998247;0.008893rad)
  LinkedObject = -> <external ../parts/steel-profile-40x40x400.FCStd>#Part
  Placement = pos=(-440,440,0) rot=(-0.01966,0.055819,0.998247;0.008893rad)
FEATURE [App::FeaturePython] Joint006  label="Fixed"  # Assembly joint (typed FeaturePython)
  Activated = true
  AngleMax = 0
  AngleMin = 0
  Detach1 = false
  Detach2 = false
  Distance = 0
  Distance2 = 0
  EnableAngleMax = false
  EnableAngleMin = false
  EnableLengthMax = false
  EnableLengthMin = false
  JointType = 0 (Fixed)
  LengthMax = 0
  LengthMin = 0
  Offset2 = pos=(0,0,0) rot=(0,0,-1;1.5708rad)
  Placement1 = pos=(20,-1e-15,0) rot=(0.707107,0,0.707107;3.14159rad)
  Placement2 = pos=(20,-1e-15,0) rot=(0.57735,0.57735,0.57735;2.0944rad)
  Reference1 = -> Assembly [steel_profile_40x40x408.Body.Edge3,steel_profile_40x40x408.Body.Edge3]
  Reference2 = -> Assembly [steel_profile_40x40x404.Body.Edge3,steel_profile_40x40x404.Body.Edge3]
FEATURE [App::FeaturePython] GroundedJoint007  # Assembly grounded joint (typed FeaturePython)
  ObjectToGround = -> steel_profile_40x40x408
  Placement = pos=(-440,440,-5.91282e-05) rot=(-0.01966,0.055819,0.998247;0.008893rad)
FEATURE [App::Link] steel_profile_40x40x411  label="steel-profile-40x40x411"
  LinkPlacement = pos=(0,440,360) rot=(0.000611,1,0.000434;4.71234rad)
  LinkedObject = -> <external ../parts/steel-profile-40x40x400.FCStd>#Part
  Placement = pos=(0,440,360) rot=(0.000611,1,0.000434;4.71234rad)
FEATURE [App::Link] steel_profile_40x40x412  label="steel-profile-40x40x412"
  LinkPlacement = pos=(0,440,400) rot=(0.714086,0.000272,-0.713488;3.14225rad)
  LinkedObject = -> <external ../parts/steel-profile-40x40x400.FCStd>#Part
  Placement = pos=(0,440,400) rot=(0.714086,0.000272,-0.713488;3.14225rad)
FEATURE [App::Link] steel_profile_40x40x413  label="steel-profile-40x40x413"
  LinkPlacement = pos=(0,0,360) rot=(-0.000373,1,0.000455;4.71239rad)
  LinkedObject = -> <external ../parts/steel-profile-40x40x400.FCStd>#Part
  Placement = pos=(0,0,360) rot=(-0.000373,1,0.000455;4.71239rad)
FEATURE [App::Link] steel_profile_40x40x414  label="steel-profile-40x40x414"
  LinkPlacement = pos=(0,80,400.402) rot=(0.707403,0.000269,-0.706811;3.14225rad)
  LinkedObject = -> <external ../parts/steel-profile-40x40x400.FCStd>#Part
  Placement = pos=(0,80,400.402) rot=(0.707403,0.000269,-0.706811;3.14225rad)
FEATURE [App::FeaturePython] Joint011  label="Fixed001"  # Assembly joint (typed FeaturePython)
  Activated = true
  AngleMax = 0
  AngleMin = 0
  Detach1 = false
  Detach2 = false
  Distance = 0
  Distance2 = 0
  EnableAngleMax = false
  EnableAngleMin = false
  EnableLengthMax = false
  EnableLengthMin = false
  JointType = 0 (Fixed)
  LengthMax = 0
  LengthMin = 0
  Offset2 = pos=(0,0,0) rot=(0,0,-1;1.5708rad)
  Placement1 = pos=(40,20,400) rot=(0.57735,0.57735,0.57735;4.18879rad)
  Placement2 = pos=(40,20,400) rot=(0,0.707107,0.707107;3.14159rad)
  Reference1 = -> Assembly [steel_profile_40x40x411.Body.Edge10,steel_profile_40x40x411.Body.Edge10]
  Reference2 = -> Assembly [steel_profile_40x40x408.Body.Edge10,steel_profile_40x40x408.Body.Edge10]
FEATURE [App::FeaturePython] Joint012  label="Fixed002"  # Assembly joint (typed FeaturePython)
  Activated = true
  AngleMax = 0
  AngleMin = 0
  Detach1 = false
  Detach2 = false
  Distance = 0
  Distance2 = 0
  EnableAngleMax = false
  EnableAngleMin = false
  EnableLengthMax = false
  EnableLengthMin = false
  JointType = 0 (Fixed)
  LengthMax = 0
  LengthMin = 0
  Offset2 = pos=(0,0,0) rot=(0,0,1;1.5708rad)
  Placement1 = pos=(40,20,400) rot=(0.57735,0.57735,0.57735;4.18879rad)
  Placement2 = pos=(-1e-15,20,0) rot=(-1,0,0;4.71239rad)
  Reference1 = -> Assembly [steel_profile_40x40x413.Body.Edge10,steel_profile_40x40x413.Body.Edge10]
  Reference2 = -> Assembly [steel_profile_40x40x403.Body.Edge21,steel_profile_40x40x403.Body.Edge21]
FEATURE [App::FeaturePython] GroundedJoint009  # Assembly grounded joint (typed FeaturePython)
  ObjectToGround = -> steel_profile_40x40x411
  Placement = pos=(6.13518e-06,440,360) rot=(0.000611,1,0.000434;4.71234rad)
FEATURE [App::FeaturePython] GroundedJoint011  # Assembly grounded joint (typed FeaturePython)
  ObjectToGround = -> steel_profile_40x40x413
  Placement = pos=(-3.96018e-05,6.13333e-05,360) rot=(-0.000373,1,0.000455;4.71239rad)
FEATURE [App::FeaturePython] GroundedJoint012  # Assembly grounded joint (typed FeaturePython)
  ObjectToGround = -> steel_profile_40x40x414
  Placement = pos=(0.00314416,79.9633,400.402) rot=(0.707403,0.000269,-0.706811;3.14225rad)
FEATURE [App::FeaturePython] Joint014  label="Distance010"  # Assembly joint (typed FeaturePython)
  Activated = true
  AngleMax = 0
  AngleMin = 0
  Detach1 = false
  Detach2 = false
  Distance = 0
  Distance2 = 0
  EnableAngleMax = false
  EnableAngleMin = false
  EnableLengthMax = false
  EnableLengthMin = false
  JointType = 5 (Distance)
  LengthMax = 0
  LengthMin = 0
FEATURE [App::Link] steel_profile_40x40x415  label="steel-profile-40x40x415"
  LinkPlacement = pos=(-440,40,418.3) rot=(-0.999999,0,0;1.5708rad)
  LinkedObject = -> <external ../parts/steel-profile-40x40x400.FCStd>#Part
  Placement = pos=(-440,40,418.3) rot=(-0.999999,0,0;1.5708rad)
FEATURE [App::Link] x_stepper_mounting_profile  label="x-stepper-mounting-profile"
  LinkPlacement = pos=(1.563e-13,440,354.54) rot=(0,0,-1;1.5708rad)
  LinkedObject = -> <external ../parts/x-stepper-mounting-profile.FCStd>#Part
  Placement = pos=(1.563e-13,440,354.54) rot=(0,0,-1;1.5708rad)
FEATURE [App::FeaturePython] Joint015  label="Fixed003"  # Assembly joint (typed FeaturePython)
  Activated = true
  AngleMax = 0
  AngleMin = 0
  Detach1 = false
  Detach2 = false
  Distance = 0
  Distance2 = 0
  EnableAngleMax = false
  EnableAngleMin = false
  EnableLengthMax = false
  EnableLengthMin = false
  JointType = 0 (Fixed)
  LengthMax = 0
  LengthMin = 0
  Placement1 = pos=(400,20,40) rot=(-0.57735,-0.57735,0.57735;4.18879rad)
  Placement2 = pos=(20,40,400) rot=(-0.707107,0,0.707107;3.14159rad)
  Reference1 = -> Assembly [x_stepper_mounting_profile.Body.Edge22,x_stepper_mounting_profile.Body.Edge22]
  Reference2 = -> Assembly [steel_profile_40x40x400.Body.Edge16,steel_profile_40x40x400.Body.Edge16]
FEATURE [App::FeaturePython] GroundedJoint013  # Assembly grounded joint (typed FeaturePython)
  ObjectToGround = -> steel_profile_40x40x412
  Placement = pos=(0.755161,439.295,400.39) rot=(0.714086,0.000272,-0.713488;3.14225rad)
FEATURE [Assembly::JointGroup] Joints
  Group = -> [GroundedJoint,GroundedJoint001,GroundedJoint002,GroundedJoint003,GroundedJoint004,Joint,Joint001,Joint002,Joint003,Joint004,Joint005,GroundedJoint005,GroundedJoint006,Joint006,GroundedJoint007,Joint011,Joint012,GroundedJoint009,GroundedJoint011,GroundedJoint012,Joint014,GroundedJoint013,Joint015]
FEATURE [Assembly::AssemblyObject] Assembly  label="legs"
  Group = -> [Joints,steel_profile_40x40x400,GroundedJoint,steel_profile_40x40x401,steel_profile_40x40x402,steel_profile_40x40x403,steel_profile_40x40x404,steel_profile_40x40x405,steel_profile_40x40x406,steel_profile_40x40x407,GroundedJoint001,GroundedJoint002,GroundedJoint003,GroundedJoint004,Joint,Joint001,Joint002,Joint003,Joint004,Joint005,GroundedJoint005,GroundedJoint006,steel_profile_40x40x408,Joint006,+15 more]
  Origin = -> Origin
  Type = Assembly
---- part ../sub-assemblies/top-frame.FCStd = doc fcstd_4aedae5da26d ----
FCSTD DOCUMENT  (FreeCAD 1.0R39319 (Git))
Label: top-frame
License: All rights reserved
LicenseURL: http://en.wikipedia.org/wiki/All_rights_reserved
objects: App::Link×7, App::FeaturePython×7, Assembly::JointGroup×1, Assembly::AssemblyObject×1
EXTERNAL_REF file=../parts/steel-profile-40x40x400.FCStd obj=Part

FEATURE [App::Link] steel_profile_40x40x400  label="steel-profile-40x40x400"
  LinkedObject = -> <external ../parts/steel-profile-40x40x400.FCStd>#Part
FEATURE [App::FeaturePython] GroundedJoint  # Assembly grounded joint (typed FeaturePython)
  ObjectToGround = -> steel_profile_40x40x400
FEATURE [App::Link] steel_profile_40x40x401  label="steel-profile-40x40x401"
  LinkPlacement = pos=(440,0,4e-05) rot=(0,0,1;0rad)
  LinkedObject = -> <external ../parts/steel-profile-40x40x400.FCStd>#Part
  Placement = pos=(440,0,4e-05) rot=(0,0,1;0rad)
FEATURE [App::Link] steel_profile_40x40x402  label="steel-profile-40x40x402"
  LinkPlacement = pos=(0,440,0) rot=(0,0,1;0rad)
  LinkedObject = -> <external ../parts/steel-profile-40x40x400.FCStd>#Part
  Placement = pos=(0,440,0) rot=(0,0,1;0rad)
FEATURE [App::Link] steel_profile_40x40x403  label="steel-profile-40x40x403"
  LinkPlacement = pos=(440,440,0) rot=(0,0,1;0rad)
  LinkedObject = -> <external ../parts/steel-profile-40x40x400.FCStd>#Part
  Placement = pos=(440,440,0) rot=(0,0,1;0rad)
FEATURE [App::Link] steel_profile_40x40x404  label="steel-profile-40x40x404"
  LinkPlacement = pos=(40,40,376.43) rot=(0.57735,-0.57735,0.57735;4.18879rad)
  LinkedObject = -> <external ../parts/steel-profile-40x40x400.FCStd>#Part
  Placement = pos=(40,40,376.43) rot=(0.57735,-0.57735,0.57735;4.18879rad)
FEATURE [App::Link] steel_profile_40x40x405  label="steel-profile-40x40x405"
  LinkPlacement = pos=(440,440,360) rot=(0,-1,0;1.5708rad)
  LinkedObject = -> <external ../parts/steel-profile-40x40x400.FCStd>#Part
  Placement = pos=(440,440,360) rot=(0,-1,0;1.5708rad)
FEATURE [App::FeaturePython] GroundedJoint002  # Assembly grounded joint (typed FeaturePython)
  ObjectToGround = -> steel_profile_40x40x401
  Placement = pos=(440,0,4e-05) rot=(0,0,1;0rad)
FEATURE [App::FeaturePython] GroundedJoint006  # Assembly grounded joint (typed FeaturePython)
  ObjectToGround = -> steel_profile_40x40x402
  Placement = pos=(0,440,0) rot=(0,0,1;0rad)
FEATURE [App::FeaturePython] GroundedJoint007  # Assembly grounded joint (typed FeaturePython)
  ObjectToGround = -> steel_profile_40x40x403
  Placement = pos=(440,440,0) rot=(0,0,1;0rad)
FEATURE [App::FeaturePython] GroundedJoint008  # Assembly grounded joint (typed FeaturePython)
  ObjectToGround = -> steel_profile_40x40x405
  Placement = pos=(440,440,360) rot=(0,-1,0;1.5708rad)
FEATURE [App::Link] steel_profile_40x40x406  label="steel-profile-40x40x406"
  LinkPlacement = pos=(3,40,400) rot=(1,0,0;4.71239rad)
  LinkedObject = -> <external ../parts/steel-profile-40x40x400.FCStd>#Part
  Placement = pos=(3,40,400) rot=(1,0,0;4.71239rad)
FEATURE [App::FeaturePython] Joint  label="Parallel"  # Assembly joint (typed FeaturePython)
  Activated = true
  AngleMax = 0
  AngleMin = 0
  Detach1 = false
  Detach2 = false
  Distance = 0
  Distance2 = 0
  EnableAngleMax = false
  EnableAngleMin = false
  EnableLengthMax = false
  EnableLengthMin = false
  JointType = 6 (Parallel)
  LengthMax = 0
  LengthMin = 0
  Placement1 = pos=(40,20,200) rot=(-0.57735,-0.57735,0.57735;2.0944rad)
  Placement2 = pos=(40,20,200) rot=(-0.57735,-0.57735,0.57735;2.0944rad)
  Reference1 = -> Assembly [steel_profile_40x40x406.Body.Face3,steel_profile_40x40x406.Body.Face3]
  Reference2 = -> Assembly [steel_profile_40x40x402.Body.Face3,steel_profile_40x40x402.Body.Face3]
FEATURE [App::FeaturePython] GroundedJoint009  # Assembly grounded joint (typed FeaturePython)
  ObjectToGround = -> steel_profile_40x40x404
  Placement = pos=(40,40,376.43) rot=(0.57735,-0.57735,0.57735;4.18879rad)
FEATURE [Assembly::JointGroup] Joints
  Group = -> [GroundedJoint,GroundedJoint002,GroundedJoint006,GroundedJoint007,GroundedJoint008,Joint,GroundedJoint009]
FEATURE [Assembly::AssemblyObject] Assembly  label="top-frame"
  Group = -> [Joints,steel_profile_40x40x400,GroundedJoint,steel_profile_40x40x401,steel_profile_40x40x402,steel_profile_40x40x403,steel_profile_40x40x404,steel_profile_40x40x405,GroundedJoint002,GroundedJoint006,GroundedJoint007,GroundedJoint008,steel_profile_40x40x406,Joint,GroundedJoint009]
  Origin = -> Origin
  Type = Assembly
